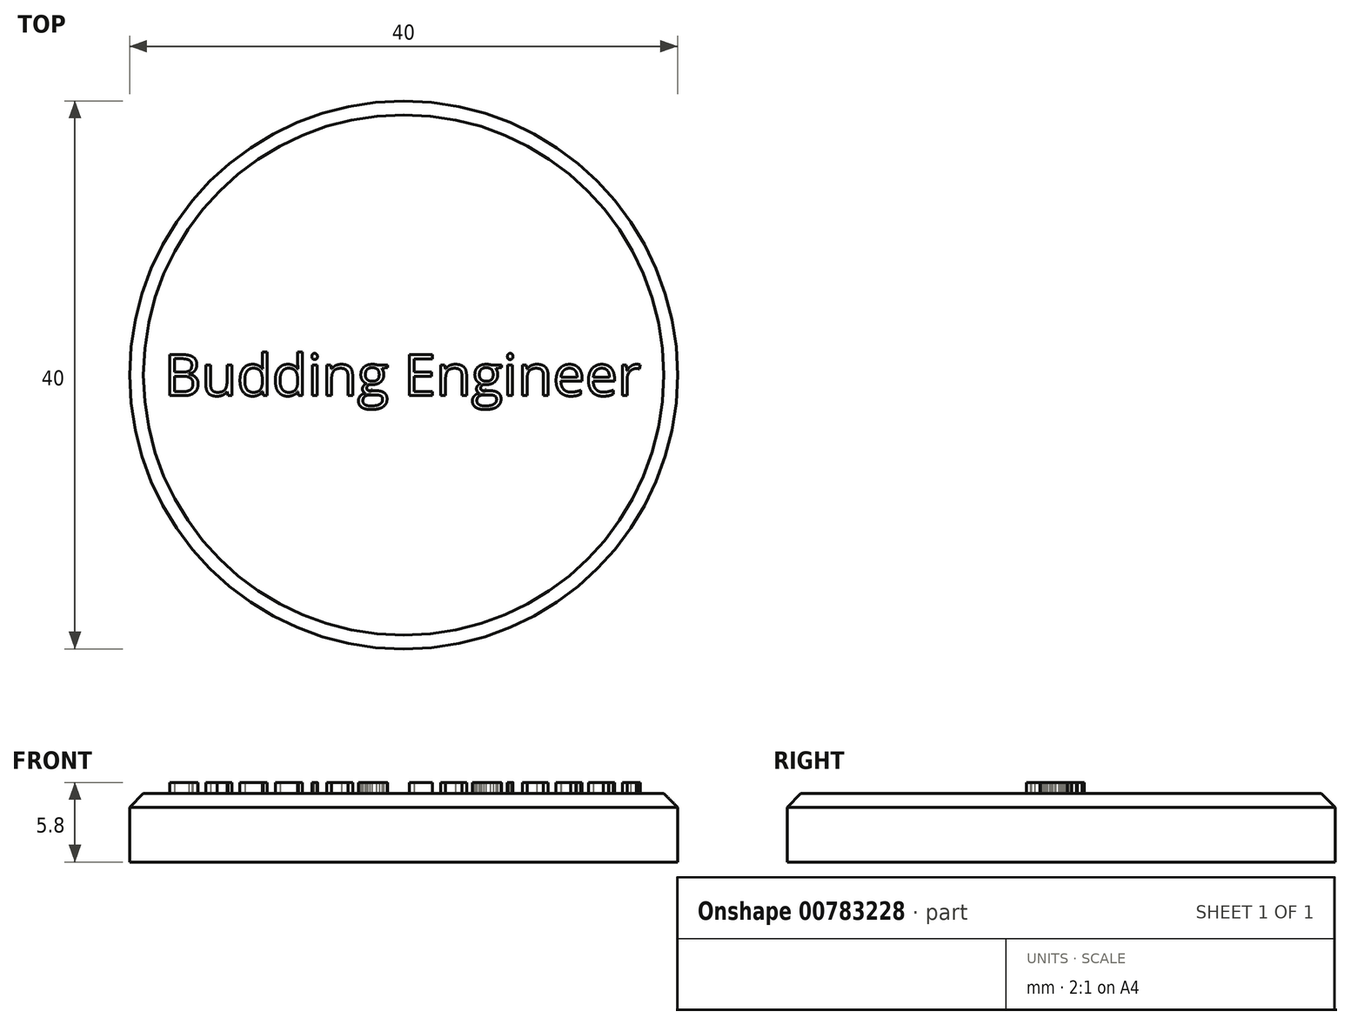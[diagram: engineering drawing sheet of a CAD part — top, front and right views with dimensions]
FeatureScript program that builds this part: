
annotation { "Feature Type Name" : "Feature", "Feature Type Description" : "" }
export const myFeature = defineFeature(function(context is Context, id is Id, definition is map)
    precondition{}
    {
        {
            var Q0;
            Q0=qCreatedBy(makeId("Top.planeOp"),FACE);
            var sketch = newSketch(context, id + "F0", { "sketchPlane" : qUnion([Q0])});
            skCircle(sketch, "E0", {"center": v(0, 0) * mm, "radius": 20 * mm});
            skLineSegment(sketch, "E1", {"start": v(-2.13, 19.89) * mm, "end": v(-1, 23) * mm});
            skLineSegment(sketch, "E2", {"start": v(-1, 23) * mm, "end": v(1, 23) * mm});
            skLineSegment(sketch, "E3", {"start": v(1, 23) * mm, "end": v(2.13, 19.89) * mm});
            skSolve(sketch);
        }
        {
            var Q0;
            {var subQ0=sQuery(id+"F0.wireOp",EDGE,"E0");var subQ1=makeQuery(id+"F0.imprint","INTERSECT",VERTEX,{"derivedFrom":[subQ0,sQuery(id+"F0.wireOp",EDGE,"E1")]});Q0=makeQuery(id+"F0.imprint","IMPRINT",FACE,{"disambiguationData":[TD([[makeQuery(id+"F0.imprint","IMPRINT",EDGE,{"disambiguationData":[TD([[subQ1,1.0]])],"derivedFrom":subQ0}),1.0]])]});}
            var Q1;
            {var subQ0=sQuery(id+"F0.wireOp",EDGE,"E1");Q1=makeQuery(id+"F0.imprint","IMPRINT",FACE,{"disambiguationData":[TD([[makeQuery(id+"F0.imprint","IMPRINT",EDGE,{"derivedFrom":subQ0}),-1.0]])]});}
            extrude(context, id + "F1", {"entities" : qUnion([Q0, Q1]), "depth" : 5 * mm, "offsetDistance" : 25 * mm});
        }
        {
            var Q0;
            Q0=makeQuery(id+"F1.opExtrude","SWEPT_BODY",BODY,{"disambiguationData":[OSD([sQuery(id+"F0.wireOp",EDGE,"E0"),sQuery(id+"F0.wireOp",EDGE,"E1"),sQuery(id+"F0.wireOp",EDGE,"E2"),sQuery(id+"F0.wireOp",EDGE,"E3")])]});
            var Q1;
            Q1=sQuery(id+"F0.wireOp",EDGE,"E0");
            circularPattern(context, id + "F2", {"operationType" : NewBodyOperationType.ADD, "entities" : qUnion([Q0]), "axis" : qUnion([Q1]), "angle" : 360 * degree, "instanceCount" : 18, "equalSpace" : true});
        }
        {
            var Q0;
            Q0=makeQuery(id+"F1.opExtrude","CAP_FACE",FACE,{"disambiguationData":[OSD([sQuery(id+"F0.wireOp",EDGE,"E0"),sQuery(id+"F0.wireOp",EDGE,"E1"),sQuery(id+"F0.wireOp",EDGE,"E2"),sQuery(id+"F0.wireOp",EDGE,"E3")])],"isStart":false});
            var sketch = newSketch(context, id + "F3", { "sketchPlane" : qUnion([Q0])});
            skText(sketch, "E4", { "text": "Budding Engineer", "fontName": "OpenSans-Regular.ttf"});
            const initialGuessF3  = {"E4": [-0.0175, -0.00151, 1, 0, 0.00303]};
            skSetInitialGuess(sketch, initialGuessF3);
            skSolve(sketch);
        }
        {
            var Q0;
            Q0 = qSketchRegion(id + "F3", true);
            extrude(context, id + "F4", {"entities" : qUnion([Q0]), "operationType" : NewBodyOperationType.ADD, "depth" : 0.8 * mm, "offsetDistance" : 25 * mm});
        }
        {
            var Q0;
            {var subQ1=sQuery(id+"F0.wireOp",EDGE,"E1");var subQ2=sQuery(id+"F0.wireOp",EDGE,"E0");Q0=makeQuery(id+"F2.boolean.opBoolean","SPLIT",EDGE,{"disambiguationData":[TD([makeQuery(id+"F2.opPattern","COPY",FACE,{"derivedFrom":makeQuery(id+"F1.opExtrude","SWEPT_FACE",FACE,{"disambiguationData":[OSD([subQ1])]}),"instanceName":"12"})])],"derivedFrom":makeQuery(id+"F1.opExtrude","CAP_EDGE",EDGE,{"disambiguationData":[OSD([subQ2])],"isStart":false})});}
            var Q1;
            Q1=makeQuery(id+"F2.opPattern","COPY",EDGE,{"derivedFrom":makeQuery(id+"F1.opExtrude","CAP_EDGE",EDGE,{"disambiguationData":[OSD([sQuery(id+"F0.wireOp",EDGE,"E1")])],"isStart":false}),"instanceName":"12"});
            var Q2;
            Q2=makeQuery(id+"F2.opPattern","COPY",EDGE,{"derivedFrom":makeQuery(id+"F1.opExtrude","CAP_EDGE",EDGE,{"disambiguationData":[OSD([sQuery(id+"F0.wireOp",EDGE,"E2")])],"isStart":false}),"instanceName":"12"});
            var Q3;
            Q3=makeQuery(id+"F2.opPattern","COPY",EDGE,{"derivedFrom":makeQuery(id+"F1.opExtrude","CAP_EDGE",EDGE,{"disambiguationData":[OSD([sQuery(id+"F0.wireOp",EDGE,"E3")])],"isStart":false}),"instanceName":"12"});
            var Q4;
            {var subQ1=sQuery(id+"F0.wireOp",EDGE,"E1");var subQ2=sQuery(id+"F0.wireOp",EDGE,"E0");Q4=makeQuery(id+"F2.boolean.opBoolean","SPLIT",EDGE,{"disambiguationData":[TD([makeQuery(id+"F2.opPattern","COPY",FACE,{"derivedFrom":makeQuery(id+"F1.opExtrude","SWEPT_FACE",FACE,{"disambiguationData":[OSD([subQ1])]}),"instanceName":"11"})])],"derivedFrom":makeQuery(id+"F1.opExtrude","CAP_EDGE",EDGE,{"disambiguationData":[OSD([subQ2])],"isStart":false})});}
            var Q5;
            Q5=makeQuery(id+"F2.opPattern","COPY",EDGE,{"derivedFrom":makeQuery(id+"F1.opExtrude","CAP_EDGE",EDGE,{"disambiguationData":[OSD([sQuery(id+"F0.wireOp",EDGE,"E1")])],"isStart":false}),"instanceName":"11"});
            var Q6;
            Q6=makeQuery(id+"F2.opPattern","COPY",EDGE,{"derivedFrom":makeQuery(id+"F1.opExtrude","CAP_EDGE",EDGE,{"disambiguationData":[OSD([sQuery(id+"F0.wireOp",EDGE,"E2")])],"isStart":false}),"instanceName":"11"});
            var Q7;
            Q7=makeQuery(id+"F2.opPattern","COPY",EDGE,{"derivedFrom":makeQuery(id+"F1.opExtrude","CAP_EDGE",EDGE,{"disambiguationData":[OSD([sQuery(id+"F0.wireOp",EDGE,"E3")])],"isStart":false}),"instanceName":"11"});
            var Q8;
            Q8=makeQuery(id+"F2.opPattern","COPY",EDGE,{"derivedFrom":makeQuery(id+"F1.opExtrude","CAP_EDGE",EDGE,{"disambiguationData":[OSD([sQuery(id+"F0.wireOp",EDGE,"E3")])],"isStart":false}),"instanceName":"13"});
            var Q9;
            Q9=makeQuery(id+"F2.opPattern","COPY",EDGE,{"derivedFrom":makeQuery(id+"F1.opExtrude","CAP_EDGE",EDGE,{"disambiguationData":[OSD([sQuery(id+"F0.wireOp",EDGE,"E2")])],"isStart":false}),"instanceName":"13"});
            var Q10;
            Q10=makeQuery(id+"F2.opPattern","COPY",EDGE,{"derivedFrom":makeQuery(id+"F1.opExtrude","CAP_EDGE",EDGE,{"disambiguationData":[OSD([sQuery(id+"F0.wireOp",EDGE,"E1")])],"isStart":false}),"instanceName":"13"});
            var Q11;
            {var subQ1=sQuery(id+"F0.wireOp",EDGE,"E1");var subQ2=sQuery(id+"F0.wireOp",EDGE,"E0");Q11=makeQuery(id+"F2.boolean.opBoolean","SPLIT",EDGE,{"disambiguationData":[TD([makeQuery(id+"F2.opPattern","COPY",FACE,{"derivedFrom":makeQuery(id+"F1.opExtrude","SWEPT_FACE",FACE,{"disambiguationData":[OSD([subQ1])]}),"instanceName":"13"})])],"derivedFrom":makeQuery(id+"F1.opExtrude","CAP_EDGE",EDGE,{"disambiguationData":[OSD([subQ2])],"isStart":false})});}
            var Q12;
            Q12=makeQuery(id+"F2.opPattern","COPY",EDGE,{"derivedFrom":makeQuery(id+"F1.opExtrude","CAP_EDGE",EDGE,{"disambiguationData":[OSD([sQuery(id+"F0.wireOp",EDGE,"E3")])],"isStart":false}),"instanceName":"14"});
            var Q13;
            Q13=makeQuery(id+"F2.opPattern","COPY",EDGE,{"derivedFrom":makeQuery(id+"F1.opExtrude","CAP_EDGE",EDGE,{"disambiguationData":[OSD([sQuery(id+"F0.wireOp",EDGE,"E2")])],"isStart":false}),"instanceName":"14"});
            var Q14;
            Q14=makeQuery(id+"F2.opPattern","COPY",EDGE,{"derivedFrom":makeQuery(id+"F1.opExtrude","CAP_EDGE",EDGE,{"disambiguationData":[OSD([sQuery(id+"F0.wireOp",EDGE,"E1")])],"isStart":false}),"instanceName":"14"});
            var Q15;
            {var subQ1=sQuery(id+"F0.wireOp",EDGE,"E1");var subQ2=sQuery(id+"F0.wireOp",EDGE,"E0");Q15=makeQuery(id+"F2.boolean.opBoolean","SPLIT",EDGE,{"disambiguationData":[TD([makeQuery(id+"F2.opPattern","COPY",FACE,{"derivedFrom":makeQuery(id+"F1.opExtrude","SWEPT_FACE",FACE,{"disambiguationData":[OSD([subQ1])]}),"instanceName":"14"})])],"derivedFrom":makeQuery(id+"F1.opExtrude","CAP_EDGE",EDGE,{"disambiguationData":[OSD([subQ2])],"isStart":false})});}
            var Q16;
            Q16=makeQuery(id+"F2.opPattern","COPY",EDGE,{"derivedFrom":makeQuery(id+"F1.opExtrude","CAP_EDGE",EDGE,{"disambiguationData":[OSD([sQuery(id+"F0.wireOp",EDGE,"E3")])],"isStart":false}),"instanceName":"15"});
            var Q17;
            Q17=makeQuery(id+"F2.opPattern","COPY",EDGE,{"derivedFrom":makeQuery(id+"F1.opExtrude","CAP_EDGE",EDGE,{"disambiguationData":[OSD([sQuery(id+"F0.wireOp",EDGE,"E2")])],"isStart":false}),"instanceName":"15"});
            var Q18;
            Q18=makeQuery(id+"F2.opPattern","COPY",EDGE,{"derivedFrom":makeQuery(id+"F1.opExtrude","CAP_EDGE",EDGE,{"disambiguationData":[OSD([sQuery(id+"F0.wireOp",EDGE,"E1")])],"isStart":false}),"instanceName":"15"});
            var Q19;
            {var subQ1=sQuery(id+"F0.wireOp",EDGE,"E1");var subQ2=sQuery(id+"F0.wireOp",EDGE,"E0");Q19=makeQuery(id+"F2.boolean.opBoolean","SPLIT",EDGE,{"disambiguationData":[TD([makeQuery(id+"F2.opPattern","COPY",FACE,{"derivedFrom":makeQuery(id+"F1.opExtrude","SWEPT_FACE",FACE,{"disambiguationData":[OSD([subQ1])]}),"instanceName":"15"})])],"derivedFrom":makeQuery(id+"F1.opExtrude","CAP_EDGE",EDGE,{"disambiguationData":[OSD([subQ2])],"isStart":false})});}
            var Q20;
            Q20=makeQuery(id+"F2.opPattern","COPY",EDGE,{"derivedFrom":makeQuery(id+"F1.opExtrude","CAP_EDGE",EDGE,{"disambiguationData":[OSD([sQuery(id+"F0.wireOp",EDGE,"E3")])],"isStart":false}),"instanceName":"16"});
            var Q21;
            Q21=makeQuery(id+"F2.opPattern","COPY",EDGE,{"derivedFrom":makeQuery(id+"F1.opExtrude","CAP_EDGE",EDGE,{"disambiguationData":[OSD([sQuery(id+"F0.wireOp",EDGE,"E2")])],"isStart":false}),"instanceName":"16"});
            var Q22;
            Q22=makeQuery(id+"F2.opPattern","COPY",EDGE,{"derivedFrom":makeQuery(id+"F1.opExtrude","CAP_EDGE",EDGE,{"disambiguationData":[OSD([sQuery(id+"F0.wireOp",EDGE,"E1")])],"isStart":false}),"instanceName":"16"});
            var Q23;
            {var subQ1=sQuery(id+"F0.wireOp",EDGE,"E1");var subQ2=sQuery(id+"F0.wireOp",EDGE,"E0");Q23=makeQuery(id+"F2.boolean.opBoolean","SPLIT",EDGE,{"disambiguationData":[TD([makeQuery(id+"F2.opPattern","COPY",FACE,{"derivedFrom":makeQuery(id+"F1.opExtrude","SWEPT_FACE",FACE,{"disambiguationData":[OSD([subQ1])]}),"instanceName":"16"})])],"derivedFrom":makeQuery(id+"F1.opExtrude","CAP_EDGE",EDGE,{"disambiguationData":[OSD([subQ2])],"isStart":false})});}
            var Q24;
            Q24=makeQuery(id+"F2.opPattern","COPY",EDGE,{"derivedFrom":makeQuery(id+"F1.opExtrude","CAP_EDGE",EDGE,{"disambiguationData":[OSD([sQuery(id+"F0.wireOp",EDGE,"E3")])],"isStart":false}),"instanceName":"17"});
            var Q25;
            Q25=makeQuery(id+"F2.opPattern","COPY",EDGE,{"derivedFrom":makeQuery(id+"F1.opExtrude","CAP_EDGE",EDGE,{"disambiguationData":[OSD([sQuery(id+"F0.wireOp",EDGE,"E1")])],"isStart":false}),"instanceName":"17"});
            var Q26;
            {var subQ0=sQuery(id+"F0.wireOp",EDGE,"E3");var subQ2=sQuery(id+"F0.wireOp",EDGE,"E0");Q26=makeQuery(id+"F2.boolean.opBoolean","SPLIT",EDGE,{"disambiguationData":[TD([makeQuery(id+"F1.opExtrude","SWEPT_FACE",FACE,{"disambiguationData":[OSD([subQ0])]})])],"derivedFrom":makeQuery(id+"F1.opExtrude","CAP_EDGE",EDGE,{"disambiguationData":[OSD([subQ2])],"isStart":false})});}
            var Q27;
            Q27=makeQuery(id+"F1.opExtrude","CAP_EDGE",EDGE,{"disambiguationData":[OSD([sQuery(id+"F0.wireOp",EDGE,"E3")])],"isStart":false});
            var Q28;
            Q28=makeQuery(id+"F1.opExtrude","CAP_EDGE",EDGE,{"disambiguationData":[OSD([sQuery(id+"F0.wireOp",EDGE,"E1")])],"isStart":false});
            var Q29;
            {var subQ1=sQuery(id+"F0.wireOp",EDGE,"E1");var subQ2=sQuery(id+"F0.wireOp",EDGE,"E0");Q29=makeQuery(id+"F2.boolean.opBoolean","SPLIT",EDGE,{"disambiguationData":[TD([makeQuery(id+"F1.opExtrude","SWEPT_FACE",FACE,{"disambiguationData":[OSD([subQ1])]})])],"derivedFrom":makeQuery(id+"F1.opExtrude","CAP_EDGE",EDGE,{"disambiguationData":[OSD([subQ2])],"isStart":false})});}
            var Q30;
            Q30=makeQuery(id+"F2.opPattern","COPY",EDGE,{"derivedFrom":makeQuery(id+"F1.opExtrude","CAP_EDGE",EDGE,{"disambiguationData":[OSD([sQuery(id+"F0.wireOp",EDGE,"E3")])],"isStart":false}),"instanceName":"1"});
            var Q31;
            Q31=makeQuery(id+"F2.opPattern","COPY",EDGE,{"derivedFrom":makeQuery(id+"F1.opExtrude","CAP_EDGE",EDGE,{"disambiguationData":[OSD([sQuery(id+"F0.wireOp",EDGE,"E1")])],"isStart":false}),"instanceName":"1"});
            var Q32;
            {var subQ1=sQuery(id+"F0.wireOp",EDGE,"E1");var subQ2=sQuery(id+"F0.wireOp",EDGE,"E0");Q32=makeQuery(id+"F2.boolean.opBoolean","SPLIT",EDGE,{"disambiguationData":[TD([makeQuery(id+"F2.opPattern","COPY",FACE,{"derivedFrom":makeQuery(id+"F1.opExtrude","SWEPT_FACE",FACE,{"disambiguationData":[OSD([subQ1])]}),"instanceName":"1"})])],"derivedFrom":makeQuery(id+"F1.opExtrude","CAP_EDGE",EDGE,{"disambiguationData":[OSD([subQ2])],"isStart":false})});}
            var Q33;
            Q33=makeQuery(id+"F2.opPattern","COPY",EDGE,{"derivedFrom":makeQuery(id+"F1.opExtrude","CAP_EDGE",EDGE,{"disambiguationData":[OSD([sQuery(id+"F0.wireOp",EDGE,"E3")])],"isStart":false}),"instanceName":"2"});
            var Q34;
            Q34=makeQuery(id+"F2.opPattern","COPY",EDGE,{"derivedFrom":makeQuery(id+"F1.opExtrude","CAP_EDGE",EDGE,{"disambiguationData":[OSD([sQuery(id+"F0.wireOp",EDGE,"E1")])],"isStart":false}),"instanceName":"2"});
            var Q35;
            {var subQ1=sQuery(id+"F0.wireOp",EDGE,"E1");var subQ2=sQuery(id+"F0.wireOp",EDGE,"E0");Q35=makeQuery(id+"F2.boolean.opBoolean","SPLIT",EDGE,{"disambiguationData":[TD([makeQuery(id+"F2.opPattern","COPY",FACE,{"derivedFrom":makeQuery(id+"F1.opExtrude","SWEPT_FACE",FACE,{"disambiguationData":[OSD([subQ1])]}),"instanceName":"2"})])],"derivedFrom":makeQuery(id+"F1.opExtrude","CAP_EDGE",EDGE,{"disambiguationData":[OSD([subQ2])],"isStart":false})});}
            var Q36;
            Q36=makeQuery(id+"F2.opPattern","COPY",EDGE,{"derivedFrom":makeQuery(id+"F1.opExtrude","CAP_EDGE",EDGE,{"disambiguationData":[OSD([sQuery(id+"F0.wireOp",EDGE,"E3")])],"isStart":false}),"instanceName":"3"});
            var Q37;
            Q37=makeQuery(id+"F2.opPattern","COPY",EDGE,{"derivedFrom":makeQuery(id+"F1.opExtrude","CAP_EDGE",EDGE,{"disambiguationData":[OSD([sQuery(id+"F0.wireOp",EDGE,"E1")])],"isStart":false}),"instanceName":"3"});
            var Q38;
            {var subQ1=sQuery(id+"F0.wireOp",EDGE,"E1");var subQ2=sQuery(id+"F0.wireOp",EDGE,"E0");Q38=makeQuery(id+"F2.boolean.opBoolean","SPLIT",EDGE,{"disambiguationData":[TD([makeQuery(id+"F2.opPattern","COPY",FACE,{"derivedFrom":makeQuery(id+"F1.opExtrude","SWEPT_FACE",FACE,{"disambiguationData":[OSD([subQ1])]}),"instanceName":"3"})])],"derivedFrom":makeQuery(id+"F1.opExtrude","CAP_EDGE",EDGE,{"disambiguationData":[OSD([subQ2])],"isStart":false})});}
            var Q39;
            Q39=makeQuery(id+"F2.opPattern","COPY",EDGE,{"derivedFrom":makeQuery(id+"F1.opExtrude","CAP_EDGE",EDGE,{"disambiguationData":[OSD([sQuery(id+"F0.wireOp",EDGE,"E3")])],"isStart":false}),"instanceName":"4"});
            var Q40;
            Q40=makeQuery(id+"F2.opPattern","COPY",EDGE,{"derivedFrom":makeQuery(id+"F1.opExtrude","CAP_EDGE",EDGE,{"disambiguationData":[OSD([sQuery(id+"F0.wireOp",EDGE,"E2")])],"isStart":false}),"instanceName":"4"});
            var Q41;
            Q41=makeQuery(id+"F2.opPattern","COPY",EDGE,{"derivedFrom":makeQuery(id+"F1.opExtrude","CAP_EDGE",EDGE,{"disambiguationData":[OSD([sQuery(id+"F0.wireOp",EDGE,"E1")])],"isStart":false}),"instanceName":"4"});
            var Q42;
            Q42=makeQuery(id+"F2.opPattern","COPY",EDGE,{"derivedFrom":makeQuery(id+"F1.opExtrude","CAP_EDGE",EDGE,{"disambiguationData":[OSD([sQuery(id+"F0.wireOp",EDGE,"E2")])],"isStart":false}),"instanceName":"3"});
            var Q43;
            Q43=makeQuery(id+"F2.opPattern","COPY",EDGE,{"derivedFrom":makeQuery(id+"F1.opExtrude","CAP_EDGE",EDGE,{"disambiguationData":[OSD([sQuery(id+"F0.wireOp",EDGE,"E2")])],"isStart":false}),"instanceName":"2"});
            var Q44;
            Q44=makeQuery(id+"F2.opPattern","COPY",EDGE,{"derivedFrom":makeQuery(id+"F1.opExtrude","CAP_EDGE",EDGE,{"disambiguationData":[OSD([sQuery(id+"F0.wireOp",EDGE,"E2")])],"isStart":false}),"instanceName":"1"});
            var Q45;
            Q45=makeQuery(id+"F1.opExtrude","CAP_EDGE",EDGE,{"disambiguationData":[OSD([sQuery(id+"F0.wireOp",EDGE,"E2")])],"isStart":false});
            var Q46;
            Q46=makeQuery(id+"F2.opPattern","COPY",EDGE,{"derivedFrom":makeQuery(id+"F1.opExtrude","CAP_EDGE",EDGE,{"disambiguationData":[OSD([sQuery(id+"F0.wireOp",EDGE,"E2")])],"isStart":false}),"instanceName":"17"});
            var Q47;
            {var subQ1=sQuery(id+"F0.wireOp",EDGE,"E1");var subQ2=sQuery(id+"F0.wireOp",EDGE,"E0");Q47=makeQuery(id+"F2.boolean.opBoolean","SPLIT",EDGE,{"disambiguationData":[TD([makeQuery(id+"F2.opPattern","COPY",FACE,{"derivedFrom":makeQuery(id+"F1.opExtrude","SWEPT_FACE",FACE,{"disambiguationData":[OSD([subQ1])]}),"instanceName":"4"})])],"derivedFrom":makeQuery(id+"F1.opExtrude","CAP_EDGE",EDGE,{"disambiguationData":[OSD([subQ2])],"isStart":false})});}
            var Q48;
            Q48=makeQuery(id+"F2.opPattern","COPY",EDGE,{"derivedFrom":makeQuery(id+"F1.opExtrude","CAP_EDGE",EDGE,{"disambiguationData":[OSD([sQuery(id+"F0.wireOp",EDGE,"E3")])],"isStart":false}),"instanceName":"5"});
            var Q49;
            Q49=makeQuery(id+"F2.opPattern","COPY",EDGE,{"derivedFrom":makeQuery(id+"F1.opExtrude","CAP_EDGE",EDGE,{"disambiguationData":[OSD([sQuery(id+"F0.wireOp",EDGE,"E2")])],"isStart":false}),"instanceName":"5"});
            var Q50;
            Q50=makeQuery(id+"F2.opPattern","COPY",EDGE,{"derivedFrom":makeQuery(id+"F1.opExtrude","CAP_EDGE",EDGE,{"disambiguationData":[OSD([sQuery(id+"F0.wireOp",EDGE,"E1")])],"isStart":false}),"instanceName":"5"});
            var Q51;
            {var subQ1=sQuery(id+"F0.wireOp",EDGE,"E1");var subQ2=sQuery(id+"F0.wireOp",EDGE,"E0");Q51=makeQuery(id+"F2.boolean.opBoolean","SPLIT",EDGE,{"disambiguationData":[TD([makeQuery(id+"F2.opPattern","COPY",FACE,{"derivedFrom":makeQuery(id+"F1.opExtrude","SWEPT_FACE",FACE,{"disambiguationData":[OSD([subQ1])]}),"instanceName":"5"})])],"derivedFrom":makeQuery(id+"F1.opExtrude","CAP_EDGE",EDGE,{"disambiguationData":[OSD([subQ2])],"isStart":false})});}
            var Q52;
            Q52=makeQuery(id+"F2.opPattern","COPY",EDGE,{"derivedFrom":makeQuery(id+"F1.opExtrude","CAP_EDGE",EDGE,{"disambiguationData":[OSD([sQuery(id+"F0.wireOp",EDGE,"E3")])],"isStart":false}),"instanceName":"6"});
            var Q53;
            Q53=makeQuery(id+"F2.opPattern","COPY",EDGE,{"derivedFrom":makeQuery(id+"F1.opExtrude","CAP_EDGE",EDGE,{"disambiguationData":[OSD([sQuery(id+"F0.wireOp",EDGE,"E2")])],"isStart":false}),"instanceName":"6"});
            var Q54;
            Q54=makeQuery(id+"F2.opPattern","COPY",EDGE,{"derivedFrom":makeQuery(id+"F1.opExtrude","CAP_EDGE",EDGE,{"disambiguationData":[OSD([sQuery(id+"F0.wireOp",EDGE,"E1")])],"isStart":false}),"instanceName":"6"});
            var Q55;
            {var subQ1=sQuery(id+"F0.wireOp",EDGE,"E1");var subQ2=sQuery(id+"F0.wireOp",EDGE,"E0");Q55=makeQuery(id+"F2.boolean.opBoolean","SPLIT",EDGE,{"disambiguationData":[TD([makeQuery(id+"F2.opPattern","COPY",FACE,{"derivedFrom":makeQuery(id+"F1.opExtrude","SWEPT_FACE",FACE,{"disambiguationData":[OSD([subQ1])]}),"instanceName":"6"})])],"derivedFrom":makeQuery(id+"F1.opExtrude","CAP_EDGE",EDGE,{"disambiguationData":[OSD([subQ2])],"isStart":false})});}
            var Q56;
            Q56=makeQuery(id+"F2.opPattern","COPY",EDGE,{"derivedFrom":makeQuery(id+"F1.opExtrude","CAP_EDGE",EDGE,{"disambiguationData":[OSD([sQuery(id+"F0.wireOp",EDGE,"E3")])],"isStart":false}),"instanceName":"7"});
            var Q57;
            Q57=makeQuery(id+"F2.opPattern","COPY",EDGE,{"derivedFrom":makeQuery(id+"F1.opExtrude","CAP_EDGE",EDGE,{"disambiguationData":[OSD([sQuery(id+"F0.wireOp",EDGE,"E2")])],"isStart":false}),"instanceName":"7"});
            var Q58;
            Q58=makeQuery(id+"F2.opPattern","COPY",EDGE,{"derivedFrom":makeQuery(id+"F1.opExtrude","CAP_EDGE",EDGE,{"disambiguationData":[OSD([sQuery(id+"F0.wireOp",EDGE,"E1")])],"isStart":false}),"instanceName":"7"});
            var Q59;
            {var subQ0=sQuery(id+"F0.wireOp",EDGE,"E1");var subQ2=sQuery(id+"F0.wireOp",EDGE,"E0");Q59=makeQuery(id+"F2.boolean.opBoolean","SPLIT",EDGE,{"disambiguationData":[TD([makeQuery(id+"F2.opPattern","COPY",FACE,{"derivedFrom":makeQuery(id+"F1.opExtrude","SWEPT_FACE",FACE,{"disambiguationData":[OSD([subQ0])]}),"instanceName":"7"})])],"derivedFrom":makeQuery(id+"F1.opExtrude","CAP_EDGE",EDGE,{"disambiguationData":[OSD([subQ2])],"isStart":false})});}
            var Q60;
            Q60=makeQuery(id+"F2.opPattern","COPY",EDGE,{"derivedFrom":makeQuery(id+"F1.opExtrude","CAP_EDGE",EDGE,{"disambiguationData":[OSD([sQuery(id+"F0.wireOp",EDGE,"E3")])],"isStart":false}),"instanceName":"8"});
            var Q61;
            Q61=makeQuery(id+"F2.opPattern","COPY",EDGE,{"derivedFrom":makeQuery(id+"F1.opExtrude","CAP_EDGE",EDGE,{"disambiguationData":[OSD([sQuery(id+"F0.wireOp",EDGE,"E2")])],"isStart":false}),"instanceName":"8"});
            var Q62;
            Q62=makeQuery(id+"F2.opPattern","COPY",EDGE,{"derivedFrom":makeQuery(id+"F1.opExtrude","CAP_EDGE",EDGE,{"disambiguationData":[OSD([sQuery(id+"F0.wireOp",EDGE,"E1")])],"isStart":false}),"instanceName":"8"});
            var Q63;
            {var subQ1=sQuery(id+"F0.wireOp",EDGE,"E1");var subQ2=sQuery(id+"F0.wireOp",EDGE,"E0");Q63=makeQuery(id+"F2.boolean.opBoolean","SPLIT",EDGE,{"disambiguationData":[TD([makeQuery(id+"F2.opPattern","COPY",FACE,{"derivedFrom":makeQuery(id+"F1.opExtrude","SWEPT_FACE",FACE,{"disambiguationData":[OSD([subQ1])]}),"instanceName":"8"})])],"derivedFrom":makeQuery(id+"F1.opExtrude","CAP_EDGE",EDGE,{"disambiguationData":[OSD([subQ2])],"isStart":false})});}
            var Q64;
            Q64=makeQuery(id+"F2.opPattern","COPY",EDGE,{"derivedFrom":makeQuery(id+"F1.opExtrude","CAP_EDGE",EDGE,{"disambiguationData":[OSD([sQuery(id+"F0.wireOp",EDGE,"E3")])],"isStart":false}),"instanceName":"9"});
            var Q65;
            Q65=makeQuery(id+"F2.opPattern","COPY",EDGE,{"derivedFrom":makeQuery(id+"F1.opExtrude","CAP_EDGE",EDGE,{"disambiguationData":[OSD([sQuery(id+"F0.wireOp",EDGE,"E2")])],"isStart":false}),"instanceName":"9"});
            var Q66;
            Q66=makeQuery(id+"F2.opPattern","COPY",EDGE,{"derivedFrom":makeQuery(id+"F1.opExtrude","CAP_EDGE",EDGE,{"disambiguationData":[OSD([sQuery(id+"F0.wireOp",EDGE,"E1")])],"isStart":false}),"instanceName":"9"});
            var Q67;
            {var subQ1=sQuery(id+"F0.wireOp",EDGE,"E1");var subQ2=sQuery(id+"F0.wireOp",EDGE,"E0");Q67=makeQuery(id+"F2.boolean.opBoolean","SPLIT",EDGE,{"disambiguationData":[TD([makeQuery(id+"F2.opPattern","COPY",FACE,{"derivedFrom":makeQuery(id+"F1.opExtrude","SWEPT_FACE",FACE,{"disambiguationData":[OSD([subQ1])]}),"instanceName":"9"})])],"derivedFrom":makeQuery(id+"F1.opExtrude","CAP_EDGE",EDGE,{"disambiguationData":[OSD([subQ2])],"isStart":false})});}
            var Q68;
            Q68=makeQuery(id+"F2.opPattern","COPY",EDGE,{"derivedFrom":makeQuery(id+"F1.opExtrude","CAP_EDGE",EDGE,{"disambiguationData":[OSD([sQuery(id+"F0.wireOp",EDGE,"E3")])],"isStart":false}),"instanceName":"10"});
            var Q69;
            Q69=makeQuery(id+"F2.opPattern","COPY",EDGE,{"derivedFrom":makeQuery(id+"F1.opExtrude","CAP_EDGE",EDGE,{"disambiguationData":[OSD([sQuery(id+"F0.wireOp",EDGE,"E2")])],"isStart":false}),"instanceName":"10"});
            var Q70;
            Q70=makeQuery(id+"F2.opPattern","COPY",EDGE,{"derivedFrom":makeQuery(id+"F1.opExtrude","CAP_EDGE",EDGE,{"disambiguationData":[OSD([sQuery(id+"F0.wireOp",EDGE,"E1")])],"isStart":false}),"instanceName":"10"});
            var Q71;
            {var subQ1=sQuery(id+"F0.wireOp",EDGE,"E1");var subQ2=sQuery(id+"F0.wireOp",EDGE,"E0");Q71=makeQuery(id+"F2.boolean.opBoolean","SPLIT",EDGE,{"disambiguationData":[TD([makeQuery(id+"F2.opPattern","COPY",FACE,{"derivedFrom":makeQuery(id+"F1.opExtrude","SWEPT_FACE",FACE,{"disambiguationData":[OSD([subQ1])]}),"instanceName":"10"})])],"derivedFrom":makeQuery(id+"F1.opExtrude","CAP_EDGE",EDGE,{"disambiguationData":[OSD([subQ2])],"isStart":false})});}
            chamfer(context, id + "F5", {"entities" : qUnion([Q0, Q1, Q2, Q3, Q4, Q5, Q6, Q7, Q8, Q9, Q10, Q11, Q12, Q13, Q14, Q15, Q16, Q17, Q18, Q19, Q20, Q21, Q22, Q23, Q24, Q25, Q26, Q27, Q28, Q29, Q30, Q31, Q32, Q33, Q34, Q35, Q36, Q37, Q38, Q39, Q40, Q41, Q42, Q43, Q44, Q45, Q46, Q47, Q48, Q49, Q50, Q51, Q52, Q53, Q54, Q55, Q56, Q57, Q58, Q59, Q60, Q61, Q62, Q63, Q64, Q65, Q66, Q67, Q68, Q69, Q70, Q71]), "width" : 1 * mm, "tangentPropagation" : true});
        }
    });
